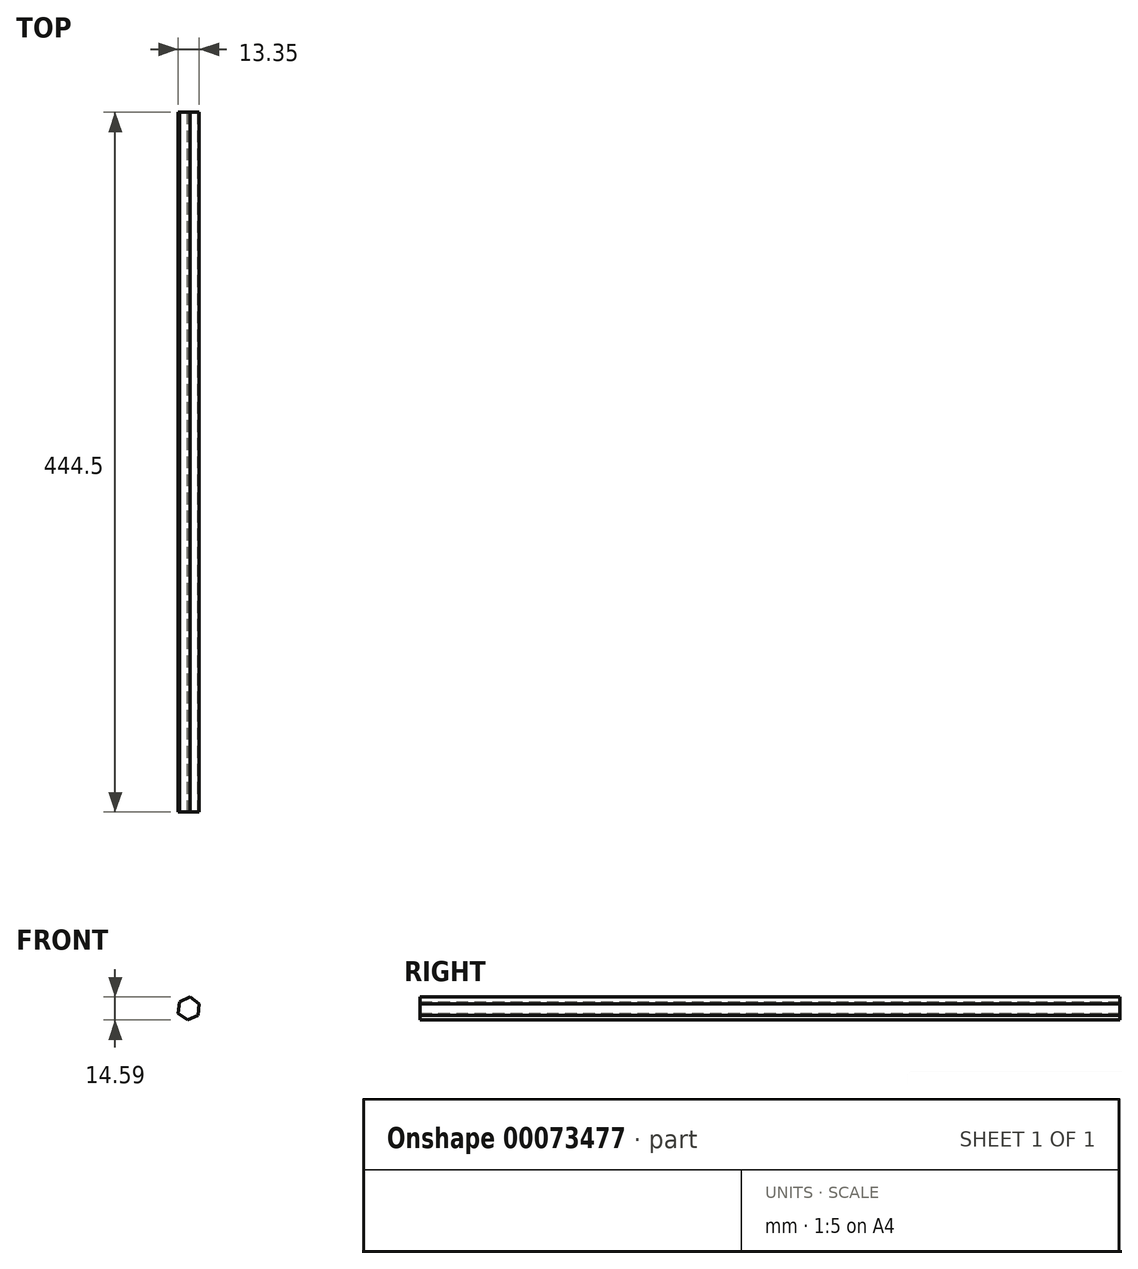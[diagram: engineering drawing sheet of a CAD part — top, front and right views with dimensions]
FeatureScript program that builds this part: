
annotation { "Feature Type Name" : "Feature", "Feature Type Description" : "" }
export const myFeature = defineFeature(function(context is Context, id is Id, definition is map)
    precondition{}
    {
        {
            var Q0;
            Q0=qCreatedBy(makeId("Front.planeOp"),FACE);
            var sketch = newSketch(context, id + "F0", { "sketchPlane" : qUnion([Q0])});
            skCircle(sketch, "E0.cCircle", {"center": v(20.7, 34.02) * mm, "radius": 6.35 * mm, "construction": true});
            skLineSegment(sketch, "E0.0", {"start": v(21.41, 41.31) * mm, "end": v(27.38, 37.05) * mm});
            skLineSegment(sketch, "E0.1", {"start": v(27.38, 37.05) * mm, "end": v(26.67, 29.75) * mm});
            skLineSegment(sketch, "E0.2", {"start": v(26.67, 29.75) * mm, "end": v(20, 26.72) * mm});
            skLineSegment(sketch, "E0.3", {"start": v(20, 26.72) * mm, "end": v(14.03, 30.98) * mm});
            skLineSegment(sketch, "E0.4", {"start": v(14.03, 30.98) * mm, "end": v(14.74, 38.28) * mm});
            skLineSegment(sketch, "E0.5", {"start": v(14.74, 38.28) * mm, "end": v(21.41, 41.31) * mm});
            skPoint(sketch, "E0.0.midPoint", {"position": v(24.4, 39.18) * mm});
            skSolve(sketch);
        }
        {
            var Q0;
            Q0=makeQuery(id+"F0.imprint","IMPRINT",FACE,{"disambiguationData":[TD([[makeQuery(id+"F0.imprint","IMPRINT",EDGE,{"derivedFrom":sQuery(id+"F0.wireOp",EDGE,"E0.0")}),-1.0]])]});
            extrude(context, id + "F1", {"entities" : qUnion([Q0]), "depth" : 444.5 * mm});
        }
    });
